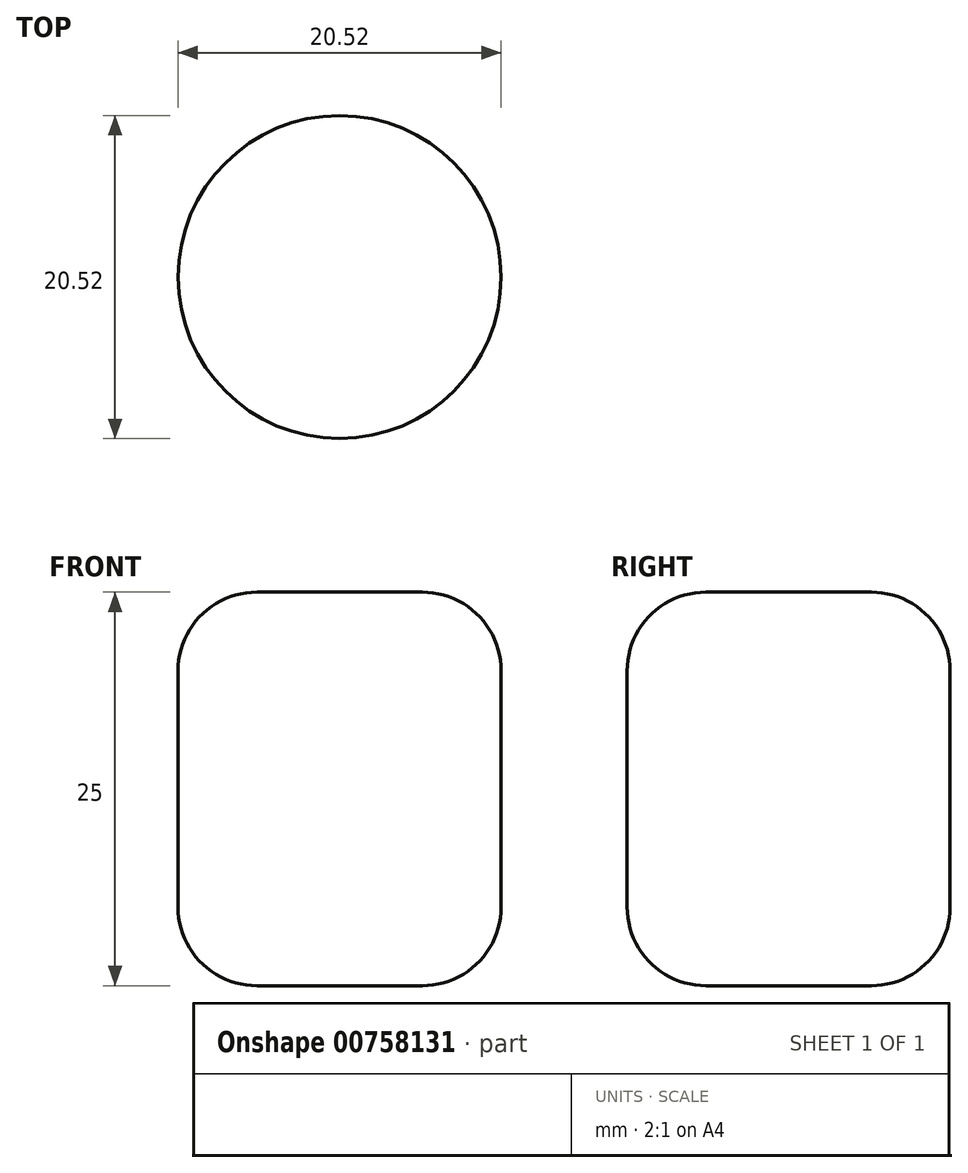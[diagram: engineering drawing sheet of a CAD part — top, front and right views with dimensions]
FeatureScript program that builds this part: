
annotation { "Feature Type Name" : "Feature", "Feature Type Description" : "" }
export const myFeature = defineFeature(function(context is Context, id is Id, definition is map)
    precondition{}
    {
        {
            var Q0;
            Q0=qCreatedBy(makeId("Top.planeOp"),FACE);
            var sketch = newSketch(context, id + "F0", { "sketchPlane" : qUnion([Q0])});
            skCircle(sketch, "E0", {"center": v(0, 0) * mm, "radius": 10.26 * mm});
            skSolve(sketch);
        }
        {
            var Q0;
            Q0 = qSketchRegion(id + "F0", true);
            extrude(context, id + "F1", {"entities" : qUnion([Q0]), "depth" : 25 * mm, "offsetDistance" : 25 * mm});
        }
        {
            var Q0;
            Q0=makeQuery(id+"F1.opExtrude","CAP_EDGE",EDGE,{"disambiguationData":[OSD([sQuery(id+"F0.wireOp",EDGE,"E0")])],"isStart":false});
            fillet(context, id + "F2", {"entities" : qUnion([Q0]), "radius" : 5 * mm, "tangentPropagation" : true, "allowEdgeOverflow" : false});
        }
        {
            var Q0;
            Q0=makeQuery(id+"F1.opExtrude","CAP_FACE",FACE,{"disambiguationData":[OSD([sQuery(id+"F0.wireOp",EDGE,"E0")])],"isStart":true});
            var Q1;
            Q1=makeQuery(id+"F1.opExtrude","CAP_EDGE",EDGE,{"disambiguationData":[OSD([sQuery(id+"F0.wireOp",EDGE,"E0")])],"isStart":true});
            fillet(context, id + "F3", {"entities" : qUnion([Q0, Q1]), "radius" : 5 * mm, "tangentPropagation" : true, "allowEdgeOverflow" : false});
        }
    });
